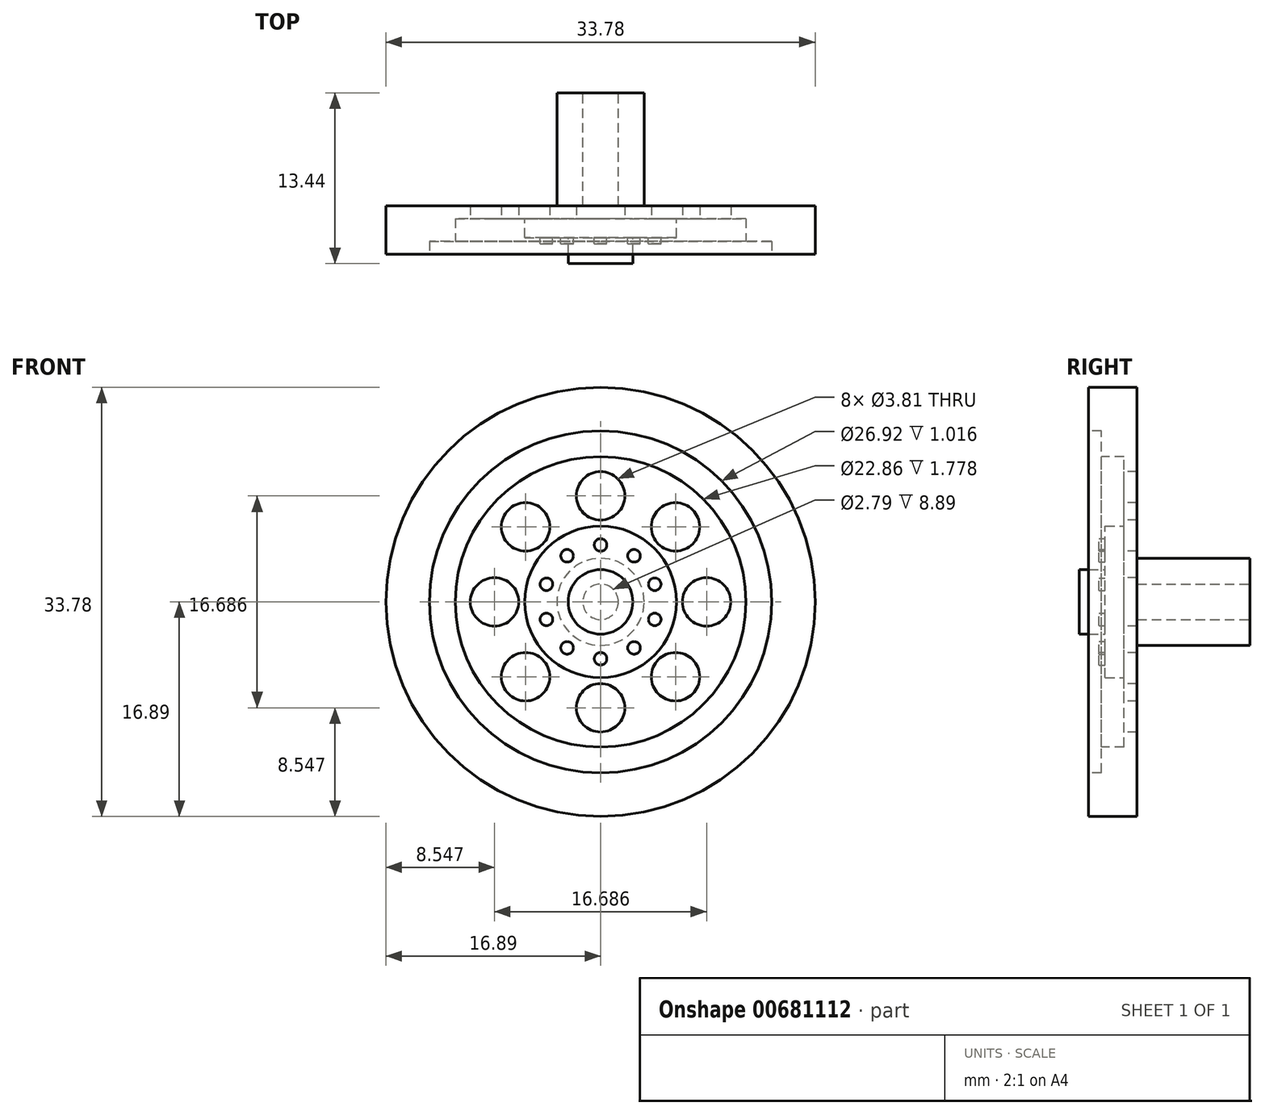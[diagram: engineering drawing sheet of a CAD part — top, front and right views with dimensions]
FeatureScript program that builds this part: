
annotation { "Feature Type Name" : "Feature", "Feature Type Description" : "" }
export const myFeature = defineFeature(function(context is Context, id is Id, definition is map)
    precondition{}
    {
        {
            var Q0;
            Q0=qCreatedBy(makeId("Front.planeOp"),FACE);
            var sketch = newSketch(context, id + "F0", { "sketchPlane" : qUnion([Q0])});
            skCircle(sketch, "E0", {"center": v(0, 0) * mm, "radius": 16.9 * mm});
            skSolve(sketch);
        }
        {
            var Q0;
            Q0=makeQuery(id+"F0.imprint","IMPRINT",FACE,{"disambiguationData":[TD([[makeQuery(id+"F0.imprint","IMPRINT",EDGE,{"derivedFrom":sQuery(id+"F0.wireOp",EDGE,"E0")}),1.0]])]});
            extrude(context, id + "F1", {"entities" : qUnion([Q0]), "oppositeDirection" : true, "depth" : 3.8 * mm, "offsetDistance" : 25.4 * mm});
        }
        {
            var Q0;
            Q0=makeQuery(id+"F1.opExtrude","CAP_FACE",FACE,{"disambiguationData":[OSD([sQuery(id+"F0.wireOp",EDGE,"E0")])],"isStart":true});
            var sketch = newSketch(context, id + "F2", { "sketchPlane" : qUnion([Q0])});
            skCircle(sketch, "E1", {"center": v(0, 0) * mm, "radius": 13.46 * mm});
            skSolve(sketch);
        }
        {
            var Q0;
            Q0=makeQuery(id+"F2.imprint","IMPRINT",FACE,{"disambiguationData":[TD([[makeQuery(id+"F2.imprint","IMPRINT",EDGE,{"derivedFrom":sQuery(id+"F2.wireOp",EDGE,"E1")}),1.0]])]});
            extrude(context, id + "F3", {"entities" : qUnion([Q0]), "operationType" : NewBodyOperationType.REMOVE, "oppositeDirection" : true, "depth" : 1.02 * mm, "offsetDistance" : 25.4 * mm});
        }
        {
            var Q0;
            Q0=makeQuery(id+"F3.boolean.opBoolean","COPY",FACE,{"derivedFrom":makeQuery(id+"F3.opExtrude","CAP_FACE",FACE,{"disambiguationData":[OSD([sQuery(id+"F2.wireOp",EDGE,"E1")])],"isStart":false})});
            var sketch = newSketch(context, id + "F4", { "sketchPlane" : qUnion([Q0])});
            skCircle(sketch, "E2", {"center": v(0, 0) * mm, "radius": 11.43 * mm});
            skSolve(sketch);
        }
        {
            var Q0;
            Q0=makeQuery(id+"F4.imprint","IMPRINT",FACE,{"disambiguationData":[TD([[makeQuery(id+"F4.imprint","IMPRINT",EDGE,{"derivedFrom":sQuery(id+"F4.wireOp",EDGE,"E2")}),1.0]])]});
            extrude(context, id + "F5", {"entities" : qUnion([Q0]), "operationType" : NewBodyOperationType.REMOVE, "oppositeDirection" : true, "depth" : 1.78 * mm, "offsetDistance" : 25.4 * mm});
        }
        {
            var Q0;
            Q0=makeQuery(id+"F5.boolean.opBoolean","COPY",FACE,{"derivedFrom":makeQuery(id+"F5.opExtrude","CAP_FACE",FACE,{"disambiguationData":[OSD([sQuery(id+"F4.wireOp",EDGE,"E2")])],"isStart":false})});
            var sketch = newSketch(context, id + "F6", { "sketchPlane" : qUnion([Q0])});
            skCircle(sketch, "E3", {"center": v(0, 8.34) * mm, "radius": 1.9 * mm});
            skCircle(sketch, "E4.1.0", {"center": v(-5.9, 5.9) * mm, "radius": 1.9 * mm});
            skCircle(sketch, "E4.2.0", {"center": v(-8.34, 0) * mm, "radius": 1.9 * mm});
            skCircle(sketch, "E4.3.0", {"center": v(-5.9, -5.9) * mm, "radius": 1.9 * mm});
            skCircle(sketch, "E4.4.0", {"center": v(0, -8.34) * mm, "radius": 1.9 * mm});
            skCircle(sketch, "E4.5.0", {"center": v(5.9, -5.9) * mm, "radius": 1.9 * mm});
            skCircle(sketch, "E4.6.0", {"center": v(8.34, 0) * mm, "radius": 1.9 * mm});
            skCircle(sketch, "E4.7.0", {"center": v(5.9, 5.9) * mm, "radius": 1.9 * mm});
            skPoint(sketch, "E4.center", {"position": v(0, 0) * mm});
            skSolve(sketch);
        }
        {
            var Q0;
            Q0=makeQuery(id+"F6.imprint","IMPRINT",FACE,{"disambiguationData":[TD([[makeQuery(id+"F6.imprint","IMPRINT",EDGE,{"derivedFrom":sQuery(id+"F6.wireOp",EDGE,"E4.1.0")}),1.0]])]});
            var Q1;
            Q1=makeQuery(id+"F6.imprint","IMPRINT",FACE,{"disambiguationData":[TD([[makeQuery(id+"F6.imprint","IMPRINT",EDGE,{"derivedFrom":sQuery(id+"F6.wireOp",EDGE,"E3")}),1.0]])]});
            var Q2;
            Q2=makeQuery(id+"F6.imprint","IMPRINT",FACE,{"disambiguationData":[TD([[makeQuery(id+"F6.imprint","IMPRINT",EDGE,{"derivedFrom":sQuery(id+"F6.wireOp",EDGE,"E4.7.0")}),1.0]])]});
            var Q3;
            Q3=makeQuery(id+"F6.imprint","IMPRINT",FACE,{"disambiguationData":[TD([[makeQuery(id+"F6.imprint","IMPRINT",EDGE,{"derivedFrom":sQuery(id+"F6.wireOp",EDGE,"E4.6.0")}),1.0]])]});
            var Q4;
            Q4=makeQuery(id+"F6.imprint","IMPRINT",FACE,{"disambiguationData":[TD([[makeQuery(id+"F6.imprint","IMPRINT",EDGE,{"derivedFrom":sQuery(id+"F6.wireOp",EDGE,"E4.5.0")}),1.0]])]});
            var Q5;
            Q5=makeQuery(id+"F6.imprint","IMPRINT",FACE,{"disambiguationData":[TD([[makeQuery(id+"F6.imprint","IMPRINT",EDGE,{"derivedFrom":sQuery(id+"F6.wireOp",EDGE,"E4.4.0")}),1.0]])]});
            var Q6;
            Q6=makeQuery(id+"F6.imprint","IMPRINT",FACE,{"disambiguationData":[TD([[makeQuery(id+"F6.imprint","IMPRINT",EDGE,{"derivedFrom":sQuery(id+"F6.wireOp",EDGE,"E4.3.0")}),1.0]])]});
            var Q7;
            Q7=makeQuery(id+"F6.imprint","IMPRINT",FACE,{"disambiguationData":[TD([[makeQuery(id+"F6.imprint","IMPRINT",EDGE,{"derivedFrom":sQuery(id+"F6.wireOp",EDGE,"E4.2.0")}),1.0]])]});
            extrude(context, id + "F7", {"entities" : qUnion([Q0, Q1, Q2, Q3, Q4, Q5, Q6, Q7]), "operationType" : NewBodyOperationType.REMOVE, "oppositeDirection" : true, "depth" : 1.98 * mm, "offsetDistance" : 25.4 * mm});
        }
        {
            var Q0;
            Q0=makeQuery(id+"F5.boolean.opBoolean","COPY",FACE,{"derivedFrom":makeQuery(id+"F5.opExtrude","CAP_FACE",FACE,{"disambiguationData":[OSD([sQuery(id+"F4.wireOp",EDGE,"E2")])],"isStart":false})});
            var sketch = newSketch(context, id + "F8", { "sketchPlane" : qUnion([Q0])});
            skCircle(sketch, "E5", {"center": v(0, 0) * mm, "radius": 5.97 * mm});
            skSolve(sketch);
        }
        {
            var Q0;
            Q0=makeQuery(id+"F8.imprint","IMPRINT",FACE,{"disambiguationData":[TD([[makeQuery(id+"F8.imprint","IMPRINT",EDGE,{"derivedFrom":sQuery(id+"F8.wireOp",EDGE,"E5")}),1.0]])]});
            extrude(context, id + "F9", {"entities" : qUnion([Q0]), "operationType" : NewBodyOperationType.ADD, "depth" : 1.5 * mm, "offsetDistance" : 25.4 * mm});
        }
        {
            var Q0;
            Q0=makeQuery(id+"F9.opExtrude","CAP_FACE",FACE,{"disambiguationData":[OSD([sQuery(id+"F8.wireOp",EDGE,"E5")])],"isStart":false});
            var sketch = newSketch(context, id + "F10", { "sketchPlane" : qUnion([Q0])});
            skCircle(sketch, "E6", {"center": v(0, 4.48) * mm, "radius": 0.5 * mm});
            skCircle(sketch, "E7.1.0", {"center": v(-2.63, 3.62) * mm, "radius": 0.5 * mm});
            skCircle(sketch, "E7.2.0", {"center": v(-4.26, 1.38) * mm, "radius": 0.5 * mm});
            skCircle(sketch, "E7.3.0", {"center": v(-4.26, -1.38) * mm, "radius": 0.5 * mm});
            skCircle(sketch, "E7.4.0", {"center": v(-2.63, -3.62) * mm, "radius": 0.5 * mm});
            skCircle(sketch, "E7.5.0", {"center": v(0, -4.48) * mm, "radius": 0.5 * mm});
            skCircle(sketch, "E7.6.0", {"center": v(2.63, -3.62) * mm, "radius": 0.5 * mm});
            skCircle(sketch, "E7.7.0", {"center": v(4.26, -1.38) * mm, "radius": 0.5 * mm});
            skCircle(sketch, "E7.8.0", {"center": v(4.26, 1.38) * mm, "radius": 0.5 * mm});
            skCircle(sketch, "E7.9.0", {"center": v(2.63, 3.62) * mm, "radius": 0.5 * mm});
            skPoint(sketch, "E7.center", {"position": v(0, 0) * mm});
            skSolve(sketch);
        }
        {
            var Q0;
            Q0=makeQuery(id+"F10.imprint","IMPRINT",FACE,{"disambiguationData":[TD([[makeQuery(id+"F10.imprint","IMPRINT",EDGE,{"derivedFrom":sQuery(id+"F10.wireOp",EDGE,"E7.1.0")}),1.0]])]});
            var Q1;
            Q1=makeQuery(id+"F10.imprint","IMPRINT",FACE,{"disambiguationData":[TD([[makeQuery(id+"F10.imprint","IMPRINT",EDGE,{"derivedFrom":sQuery(id+"F10.wireOp",EDGE,"E6")}),1.0]])]});
            var Q2;
            Q2=makeQuery(id+"F10.imprint","IMPRINT",FACE,{"disambiguationData":[TD([[makeQuery(id+"F10.imprint","IMPRINT",EDGE,{"derivedFrom":sQuery(id+"F10.wireOp",EDGE,"E7.9.0")}),1.0]])]});
            var Q3;
            Q3=makeQuery(id+"F10.imprint","IMPRINT",FACE,{"disambiguationData":[TD([[makeQuery(id+"F10.imprint","IMPRINT",EDGE,{"derivedFrom":sQuery(id+"F10.wireOp",EDGE,"E7.8.0")}),1.0]])]});
            var Q4;
            Q4=makeQuery(id+"F10.imprint","IMPRINT",FACE,{"disambiguationData":[TD([[makeQuery(id+"F10.imprint","IMPRINT",EDGE,{"derivedFrom":sQuery(id+"F10.wireOp",EDGE,"E7.7.0")}),1.0]])]});
            var Q5;
            Q5=makeQuery(id+"F10.imprint","IMPRINT",FACE,{"disambiguationData":[TD([[makeQuery(id+"F10.imprint","IMPRINT",EDGE,{"derivedFrom":sQuery(id+"F10.wireOp",EDGE,"E7.6.0")}),1.0]])]});
            var Q6;
            Q6=makeQuery(id+"F10.imprint","IMPRINT",FACE,{"disambiguationData":[TD([[makeQuery(id+"F10.imprint","IMPRINT",EDGE,{"derivedFrom":sQuery(id+"F10.wireOp",EDGE,"E7.5.0")}),1.0]])]});
            var Q7;
            Q7=makeQuery(id+"F10.imprint","IMPRINT",FACE,{"disambiguationData":[TD([[makeQuery(id+"F10.imprint","IMPRINT",EDGE,{"derivedFrom":sQuery(id+"F10.wireOp",EDGE,"E7.4.0")}),1.0]])]});
            var Q8;
            Q8=makeQuery(id+"F10.imprint","IMPRINT",FACE,{"disambiguationData":[TD([[makeQuery(id+"F10.imprint","IMPRINT",EDGE,{"derivedFrom":sQuery(id+"F10.wireOp",EDGE,"E7.3.0")}),1.0]])]});
            var Q9;
            Q9=makeQuery(id+"F10.imprint","IMPRINT",FACE,{"disambiguationData":[TD([[makeQuery(id+"F10.imprint","IMPRINT",EDGE,{"derivedFrom":sQuery(id+"F10.wireOp",EDGE,"E7.2.0")}),1.0]])]});
            extrude(context, id + "F11", {"entities" : qUnion([Q0, Q1, Q2, Q3, Q4, Q5, Q6, Q7, Q8, Q9]), "operationType" : NewBodyOperationType.ADD, "depth" : 0.48 * mm, "offsetDistance" : 25.4 * mm});
        }
        {
            var Q0;
            Q0=makeQuery(id+"F9.opExtrude","CAP_FACE",FACE,{"disambiguationData":[OSD([sQuery(id+"F8.wireOp",EDGE,"E5")])],"isStart":false});
            var sketch = newSketch(context, id + "F12", { "sketchPlane" : qUnion([Q0])});
            skCircle(sketch, "E8", {"center": v(0, 0) * mm, "radius": 2.54 * mm});
            skSolve(sketch);
        }
        {
            var Q0;
            Q0=makeQuery(id+"F12.imprint","IMPRINT",FACE,{"disambiguationData":[TD([[makeQuery(id+"F12.imprint","IMPRINT",EDGE,{"derivedFrom":sQuery(id+"F12.wireOp",EDGE,"E8")}),1.0]])]});
            var Q1;
            Q1=sQuery(id+"F12.wireOp",EDGE,"E8");
            extrude(context, id + "F13", {"entities" : qUnion([Q0]), "surfaceEntities" : qUnion([Q1]), "depth" : 2.03 * mm, "offsetDistance" : 25.4 * mm});
        }
        {
            var Q0;
            Q0=makeQuery(id+"F1.opExtrude","CAP_FACE",FACE,{"disambiguationData":[OSD([sQuery(id+"F0.wireOp",EDGE,"E0")])],"isStart":false});
            var sketch = newSketch(context, id + "F14", { "sketchPlane" : qUnion([Q0])});
            skCircle(sketch, "E9", {"center": v(0, 0) * mm, "radius": 3.43 * mm});
            skSolve(sketch);
        }
        {
            var Q0;
            Q0=makeQuery(id+"F14.imprint","IMPRINT",FACE,{"disambiguationData":[TD([[makeQuery(id+"F14.imprint","IMPRINT",EDGE,{"derivedFrom":sQuery(id+"F14.wireOp",EDGE,"E9")}),1.0]])]});
            extrude(context, id + "F15", {"entities" : qUnion([Q0]), "operationType" : NewBodyOperationType.ADD, "depth" : 8.9 * mm, "offsetDistance" : 25.4 * mm});
        }
        {
            var Q0;
            Q0=makeQuery(id+"F15.opExtrude","CAP_FACE",FACE,{"disambiguationData":[OSD([sQuery(id+"F14.wireOp",EDGE,"E9")])],"isStart":false});
            var sketch = newSketch(context, id + "F16", { "sketchPlane" : qUnion([Q0])});
            skCircle(sketch, "E10", {"center": v(0, 0) * mm, "radius": 1.4 * mm});
            skSolve(sketch);
        }
        {
            var Q0;
            Q0=makeQuery(id+"F16.imprint","IMPRINT",FACE,{"disambiguationData":[TD([[makeQuery(id+"F16.imprint","IMPRINT",EDGE,{"derivedFrom":sQuery(id+"F16.wireOp",EDGE,"E10")}),1.0]])]});
            extrude(context, id + "F17", {"entities" : qUnion([Q0]), "operationType" : NewBodyOperationType.REMOVE, "oppositeDirection" : true, "depth" : 8.9 * mm, "offsetDistance" : 25.4 * mm});
        }
    });
